# Revit family: Column-Roseburg-RigidLam_LVL
name_source: partatom
category: Structural Columns
units: mm (PartAtom-declared; Revit-internal decimal feet)

## family parameters
Always export as geometry = No
Beam cutback in plan = From bounding box
Classification Number = 23.25.30.11.14.11
Cut with Voids When Loaded = No
Material for Model Behavior = Wood
Section Shape = Not Defined
Shared = No
Show family pre-cut in plan views = Yes

## types (6) — shared parameters
Application Chart = https://www.roseburg.com
Assembly Code = B10
Building Codes = See PR-L289 & PR-L289C
EWP Application Chart = https://www.arcat.com
Installation Guide = https://www.arcat.com
Keynote = 06 40 00
Length = 60
Manufacturer = Roseburg
Material = Plywood LVL
Series = RigidLam
Structural Material = Engineered Wood - Roseburg - Plywood LVL
Testing Data = See ESR1210
URL = https://www.roseburg.com

## per-type parameters (varying)
| type | Description | b | d |
| 3-1/2" x 3-1/2" | RigidLam LVL Column - 3-1/2" x 3-1/2" | 0' - 3 1/2" | 0' - 3 1/2" |
| 3-1/2" x 5-1/4" | RigidLam LVL Column - 3-1/2" x 5-1/4" | 0' - 3 1/2" | 0' - 5 1/4" |
| 3-1/2" x 7" | RigidLam LVL Column - 3-1/2" x 7" | 0' - 3 1/2" | 0' - 7" |
| 5-1/4" x 5-1/4" | RigidLam LVL Column - 5-1/4" x 5-1/4" | 0' - 5 1/4" | 0' - 5 1/4" |
| 5-1/4" x 7" | RigidLam LVL Column - 5-1/4" x 7" | 0' - 5 1/4" | 0' - 7" |
| 7" x 7" | RigidLam LVL Column - 7" x 7" | 0' - 7" | 0' - 7" |

note: column(s) folded — value = type name in every type: Model

## geometry (parser evidence)
native form markers: Sweep x1
no freeform markers — native parametric forms only
